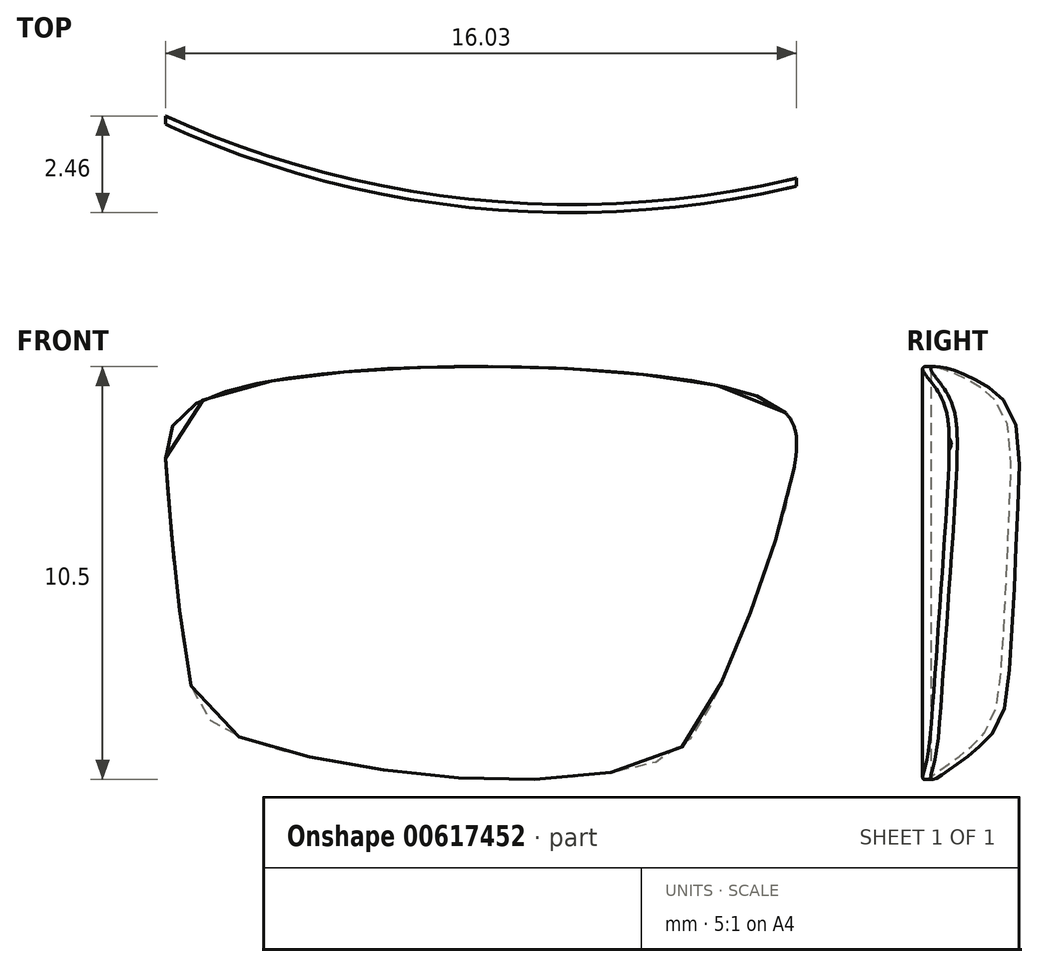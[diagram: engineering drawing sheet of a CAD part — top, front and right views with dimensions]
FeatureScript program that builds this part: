
annotation { "Feature Type Name" : "Feature", "Feature Type Description" : "" }
export const myFeature = defineFeature(function(context is Context, id is Id, definition is map)
    precondition{}
    {
        {
            var Q0;
            Q0=qCreatedBy(makeId("Front.planeOp"),FACE);
            var sketch = newSketch(context, id + "F0", { "sketchPlane" : qUnion([Q0])});
            skFitSpline(sketch, "E0", {"points": [v(-17.91, 1.87) * mm, v(-17.03, 4.08) * mm, v(-2.95, 4.2) * mm, v(-1.99, 2.4) * mm, v(-4.2, -3.82) * mm, v(-5.49, -5.1) * mm, v(-8.7, -5.54) * mm, v(-12.26, -5.32) * mm, v(-16.62, -4.2) * mm, v(-17.4, -2.77) * mm, v(-17.91, 1.87) * mm]});
            skPoint(sketch, "E1", {"position": v(-3.12, 3.22) * mm});
            skLineSegment(sketch, "E2", {"start": v(-2.2, 3.76) * mm, "end": v(-1.25, 3.76) * mm});
            skLineSegment(sketch, "E3", {"start": v(-1.04, 3.56) * mm, "end": v(-1.04, 1.8) * mm});
            skLineSegment(sketch, "E4", {"start": v(-1.15, 1.7) * mm, "end": v(-1.53, 1.7) * mm});
            skLineSegment(sketch, "E5", {"start": v(-1.63, 1.8) * mm, "end": v(-1.63, 2.64) * mm});
            skLineSegment(sketch, "E6", {"start": v(-1.67, 2.66) * mm, "end": v(-1.99, 2.4) * mm});
            skPoint(sketch, "E7.visualSharp", {"position": v(-1.04, 1.7) * mm});
            skArc(sketch, "E7.filletArc", {"start": v(-1.15, 1.7) * mm, "mid": v(-1.07, 1.72) * mm, "end": v(-1.04, 1.8) * mm});
            skPoint(sketch, "E8.visualSharp", {"position": v(-1.63, 1.7) * mm});
            skArc(sketch, "E8.filletArc", {"start": v(-1.63, 1.8) * mm, "mid": v(-1.6, 1.72) * mm, "end": v(-1.53, 1.7) * mm});
            skPoint(sketch, "E9.visualSharp", {"position": v(-1.63, 2.7) * mm});
            skArc(sketch, "E9.filletArc", {"start": v(-1.63, 2.64) * mm, "mid": v(-1.64, 2.67) * mm, "end": v(-1.67, 2.66) * mm});
            skPoint(sketch, "E10.visualSharp", {"position": v(-1.04, 3.76) * mm});
            skArc(sketch, "E10.filletArc", {"start": v(-1.04, 3.56) * mm, "mid": v(-1.1, 3.7) * mm, "end": v(-1.25, 3.76) * mm});
            skSolve(sketch);
        }
        {
            var Q0;
            Q0=qCreatedBy(makeId("Front.planeOp"),FACE);
            var sketch = newSketch(context, id + "F1", { "sketchPlane" : qUnion([Q0])});
            skFitSpline(sketch, "E11.1", {"points": [v(-17.61, 2.35) * mm, v(-17.55, 1.78) * mm, v(-17.49, 1.13) * mm, v(-17.39, 0.2) * mm, v(-17.24, -1.03) * mm, v(-17.09, -2.15) * mm, v(-16.96, -2.88) * mm, v(-16.87, -3.3) * mm, v(-16.76, -3.6) * mm, v(-16.62, -3.8) * mm, v(-16.4, -3.99) * mm, v(-16, -4.19) * mm, v(-15.47, -4.38) * mm, v(-14.85, -4.54) * mm, v(-14.16, -4.7) * mm, v(-13.2, -4.86) * mm, v(-12, -5.02) * mm, v(-10.8, -5.14) * mm, v(-9.72, -5.2) * mm, v(-8.62, -5.18) * mm, v(-7.41, -5.1) * mm, v(-6.46, -4.96) * mm, v(-5.82, -4.8) * mm, v(-5.44, -4.67) * mm, v(-5.17, -4.52) * mm, v(-4.95, -4.34) * mm, v(-4.74, -4.07) * mm, v(-4.5, -3.66) * mm, v(-4.22, -3.09) * mm, v(-3.82, -2.16) * mm, v(-3.4, -1.07) * mm, v(-3.03, 0.06) * mm, v(-2.78, 0.88) * mm, v(-2.57, 1.66) * mm, v(-2.42, 2.35) * mm, v(-2.33, 2.91) * mm, v(-2.34, 3.23) * mm, v(-2.4, 3.4) * mm, v(-2.45, 3.5) * mm, v(-2.53, 3.6) * mm, v(-2.71, 3.75) * mm, v(-3.1, 3.93) * mm, v(-3.86, 4.13) * mm, v(-4.85, 4.3) * mm, v(-6.02, 4.42) * mm, v(-7.31, 4.5) * mm, v(-9.15, 4.56) * mm, v(-11.07, 4.53) * mm, v(-12.9, 4.42) * mm, v(-14.16, 4.28) * mm, v(-15.3, 4.1) * mm, v(-16.24, 3.88) * mm, v(-16.95, 3.62) * mm, v(-17.34, 3.35) * mm, v(-17.52, 3.1) * mm, v(-17.6, 2.79) * mm, v(-17.61, 2.35) * mm, v(-17.55, 1.78) * mm, v(-17.49, 1.13) * mm]});
            skFitSpline(sketch, "E12", {"points": [v(-5.23, 4.33) * mm, v(-3.14, 3.17) * mm, v(-3.05, 0) * mm], "startDerivative": vector(6.83, -0.85) * mm, "endDerivative": vector(-2.66, -9.5) * mm});
            skFitSpline(sketch, "E13", {"points": [v(-17.5, 1.25) * mm, v(-15.83, 3.98) * mm], "startDerivative": vector(-0.72, 7.51) * mm, "endDerivative": vector(1, 0.26) * mm});
            skFitSpline(sketch, "E14", {"points": [v(-17.61, 2.35) * mm, v(-17.55, 1.78) * mm, v(-17.49, 1.13) * mm, v(-17.39, 0.2) * mm, v(-17.24, -1.03) * mm, v(-17.09, -2.15) * mm, v(-16.96, -2.88) * mm, v(-16.87, -3.3) * mm, v(-16.76, -3.6) * mm, v(-16.62, -3.8) * mm, v(-16.4, -3.99) * mm, v(-16, -4.19) * mm, v(-15.47, -4.38) * mm, v(-14.85, -4.54) * mm, v(-14.16, -4.7) * mm, v(-13.2, -4.86) * mm, v(-12, -5.02) * mm, v(-10.8, -5.14) * mm, v(-9.72, -5.2) * mm, v(-8.62, -5.18) * mm, v(-7.41, -5.1) * mm, v(-6.46, -4.96) * mm, v(-5.82, -4.8) * mm, v(-5.44, -4.67) * mm, v(-5.17, -4.52) * mm, v(-4.95, -4.34) * mm, v(-4.74, -4.07) * mm, v(-4.5, -3.66) * mm, v(-4.22, -3.09) * mm, v(-3.82, -2.16) * mm, v(-3.4, -1.07) * mm, v(-3.03, 0.06) * mm, v(-2.78, 0.88) * mm, v(-2.57, 1.66) * mm, v(-2.42, 2.35) * mm, v(-2.33, 2.91) * mm, v(-2.34, 3.23) * mm, v(-2.4, 3.4) * mm, v(-2.45, 3.5) * mm, v(-2.53, 3.6) * mm, v(-2.71, 3.75) * mm, v(-3.1, 3.93) * mm, v(-3.86, 4.13) * mm, v(-4.85, 4.3) * mm, v(-6.02, 4.42) * mm, v(-7.31, 4.5) * mm, v(-9.15, 4.56) * mm, v(-11.07, 4.53) * mm, v(-12.9, 4.42) * mm, v(-14.16, 4.28) * mm, v(-15.3, 4.1) * mm, v(-16.24, 3.88) * mm, v(-16.95, 3.62) * mm, v(-17.34, 3.35) * mm, v(-17.52, 3.1) * mm, v(-17.6, 2.79) * mm, v(-17.61, 2.35) * mm, v(-17.55, 1.78) * mm, v(-17.49, 1.13) * mm]});
            skFitSpline(sketch, "E15", {"points": [v(-3.81, -4.29) * mm, v(-1.38, 0.76) * mm, v(-1.6, 0.87) * mm, v(-1.7, 1.14) * mm, v(-0.52, 1.5) * mm], "startDerivative": vector(10.25, 18.32) * mm, "endDerivative": vector(8.4, 0.03) * mm});
            skLineSegment(sketch, "E16", {"start": v(-0.57, 4.2) * mm, "end": v(-0.57, 4.2) * mm});
            skLineSegment(sketch, "E17", {"start": v(-0.57, 4.2) * mm, "end": v(-0.57, 1.5) * mm});
            skFitSpline(sketch, "E18", {"points": [v(-0.57, 4.2) * mm, v(-1.74, 4) * mm], "startDerivative": vector(-1.49, -0.02) * mm, "endDerivative": vector(-0.6, -0.33) * mm});
            skLineSegment(sketch, "E19", {"start": v(-19.77, 3.41) * mm, "end": v(-19.75, 1.7) * mm});
            skLineSegment(sketch, "E20", {"start": v(-18.95, 1.45) * mm, "end": v(-19.5, 1.44) * mm});
            skLineSegment(sketch, "E21", {"start": v(-18.5, 3.69) * mm, "end": v(-19.52, 3.67) * mm});
            skArc(sketch, "E22.filletArc", {"start": v(-18.5, 3.69) * mm, "mid": v(-18.27, 3.74) * mm, "end": v(-18.1, 3.89) * mm});
            skPoint(sketch, "E23.visualSharp", {"position": v(-19.77, 3.67) * mm});
            skArc(sketch, "E23.filletArc", {"start": v(-19.52, 3.67) * mm, "mid": v(-19.7, 3.6) * mm, "end": v(-19.77, 3.41) * mm});
            skPoint(sketch, "E24.visualSharp", {"position": v(-19.74, 1.25) * mm});
            skArc(sketch, "E25.filletArc", {"start": v(-1.9, 4.17) * mm, "mid": v(-1.73, 4.08) * mm, "end": v(-1.53, 4.08) * mm});
            skFitSpline(sketch, "E26", {"points": [v(-18.1, 3.89) * mm, v(-17.45, 4.45) * mm, v(-12.76, 5.38) * mm, v(-4.33, 5.05) * mm, v(-2.37, 4.5) * mm], "startDerivative": vector(5.74, 6.16) * mm, "endDerivative": vector(8.17, -3.37) * mm});
            skFitSpline(sketch, "E27", {"points": [v(-3.81, -4.29) * mm, v(-4.85, -5.44) * mm, v(-10.17, -6.1) * mm, v(-15.6, -5.22) * mm, v(-17.46, -4.2) * mm, v(-18.48, 1.46) * mm], "startDerivative": vector(-7.7, -11.8) * mm, "endDerivative": vector(-2.7, 30.17) * mm});
            skArc(sketch, "E28.filletArc", {"start": v(-19.75, 1.7) * mm, "mid": v(-19.67, 1.52) * mm, "end": v(-19.5, 1.44) * mm});
            skArc(sketch, "E29.filletArc", {"start": v(-18.44, 0.99) * mm, "mid": v(-18.6, 1.32) * mm, "end": v(-18.95, 1.45) * mm});
            skArc(sketch, "E30.MirrorCS", {"start": v(18.61, 1.7) * mm, "mid": v(18.54, 1.52) * mm, "end": v(18.36, 1.45) * mm});
            skArc(sketch, "E31.MirrorCS", {"start": v(17.36, 3.69) * mm, "mid": v(17.14, 3.74) * mm, "end": v(16.96, 3.9) * mm});
            skArc(sketch, "E32.MirrorCS", {"start": v(0.76, 4.17) * mm, "mid": v(0.59, 4.08) * mm, "end": v(0.4, 4.08) * mm});
            skArc(sketch, "E33.MirrorCS", {"start": v(17.3, 1) * mm, "mid": v(17.47, 1.32) * mm, "end": v(17.82, 1.45) * mm});
            skArc(sketch, "E34.MirrorCS", {"start": v(18.39, 3.67) * mm, "mid": v(18.56, 3.6) * mm, "end": v(18.64, 3.42) * mm});
            skLineSegment(sketch, "E35.MirrorCS", {"start": v(17.82, 1.45) * mm, "end": v(18.36, 1.45) * mm});
            skFitSpline(sketch, "E36.MirrorCS", {"points": [v(-0.57, 4.2) * mm, v(0.6, 4) * mm], "startDerivative": vector(1.49, -0.02) * mm, "endDerivative": vector(0.6, -0.33) * mm});
            skLineSegment(sketch, "E37.MirrorCS", {"start": v(17.36, 3.69) * mm, "end": v(18.39, 3.67) * mm});
            skFitSpline(sketch, "E38.MirrorCS", {"points": [v(2.68, -4.29) * mm, v(3.72, -5.44) * mm, v(9.04, -6.1) * mm, v(14.47, -5.22) * mm, v(16.32, -4.2) * mm, v(17.35, 1.46) * mm], "startDerivative": vector(7.7, -11.79) * mm, "endDerivative": vector(2.69, 30.18) * mm});
            skFitSpline(sketch, "E39.MirrorCS", {"points": [v(4.1, 4.33) * mm, v(2, 3.17) * mm, v(1.92, 0) * mm], "startDerivative": vector(-6.83, -0.85) * mm, "endDerivative": vector(2.66, -9.5) * mm});
            skPoint(sketch, "E40.MirrorP", {"position": v(18.6, 1.25) * mm});
            skFitSpline(sketch, "E41.MirrorCS", {"points": [v(16.36, 1.25) * mm, v(14.7, 3.98) * mm], "startDerivative": vector(0.72, 7.51) * mm, "endDerivative": vector(-1, 0.26) * mm});
            skLineSegment(sketch, "E42.MirrorCS", {"start": v(18.64, 3.42) * mm, "end": v(18.61, 1.7) * mm});
            skFitSpline(sketch, "E43.MirrorCS", {"points": [v(16.48, 2.35) * mm, v(16.42, 1.79) * mm, v(16.35, 1.13) * mm, v(16.25, 0.2) * mm, v(16.1, -1.02) * mm, v(15.95, -2.14) * mm, v(15.83, -2.88) * mm, v(15.73, -3.3) * mm, v(15.62, -3.6) * mm, v(15.48, -3.8) * mm, v(15.26, -3.99) * mm, v(14.87, -4.19) * mm, v(14.34, -4.37) * mm, v(13.71, -4.54) * mm, v(13.03, -4.69) * mm, v(12.07, -4.86) * mm, v(10.87, -5.02) * mm, v(9.67, -5.14) * mm, v(8.58, -5.2) * mm, v(7.5, -5.18) * mm, v(6.28, -5.1) * mm, v(5.33, -4.95) * mm, v(4.69, -4.8) * mm, v(4.3, -4.67) * mm, v(4.03, -4.52) * mm, v(3.82, -4.34) * mm, v(3.6, -4.07) * mm, v(3.36, -3.66) * mm, v(3.09, -3.09) * mm, v(2.69, -2.16) * mm, v(2.27, -1.07) * mm, v(1.9, 0.06) * mm, v(1.64, 0.88) * mm, v(1.43, 1.66) * mm, v(1.28, 2.35) * mm, v(1.2, 2.91) * mm, v(1.2, 3.23) * mm, v(1.26, 3.4) * mm, v(1.31, 3.5) * mm, v(1.4, 3.6) * mm, v(1.58, 3.75) * mm, v(1.96, 3.93) * mm, v(2.73, 4.13) * mm, v(3.72, 4.3) * mm, v(4.88, 4.42) * mm, v(6.18, 4.5) * mm, v(8.02, 4.56) * mm, v(9.94, 4.54) * mm, v(11.76, 4.42) * mm, v(13.03, 4.28) * mm, v(14.16, 4.1) * mm, v(15.1, 3.88) * mm, v(15.8, 3.62) * mm, v(16.2, 3.35) * mm, v(16.38, 3.1) * mm, v(16.47, 2.79) * mm, v(16.48, 2.35) * mm, v(16.42, 1.79) * mm, v(16.35, 1.13) * mm]});
            skFitSpline(sketch, "E44.MirrorCS", {"points": [v(16.96, 3.9) * mm, v(16.3, 4.45) * mm, v(11.63, 5.39) * mm, v(3.19, 5.05) * mm, v(1.23, 4.5) * mm], "startDerivative": vector(-5.74, 6.15) * mm, "endDerivative": vector(-8.17, -3.38) * mm});
            skPoint(sketch, "E45.MirrorP", {"position": v(18.64, 3.67) * mm});
            skFitSpline(sketch, "E46.MirrorCS", {"points": [v(16.48, 2.35) * mm, v(16.42, 1.79) * mm, v(16.35, 1.13) * mm, v(16.25, 0.2) * mm, v(16.1, -1.02) * mm, v(15.95, -2.14) * mm, v(15.83, -2.88) * mm, v(15.73, -3.3) * mm, v(15.62, -3.6) * mm, v(15.48, -3.8) * mm, v(15.26, -3.99) * mm, v(14.87, -4.19) * mm, v(14.34, -4.37) * mm, v(13.71, -4.54) * mm, v(13.03, -4.69) * mm, v(12.07, -4.86) * mm, v(10.87, -5.02) * mm, v(9.67, -5.14) * mm, v(8.58, -5.2) * mm, v(7.5, -5.18) * mm, v(6.28, -5.1) * mm, v(5.33, -4.95) * mm, v(4.69, -4.8) * mm, v(4.3, -4.67) * mm, v(4.03, -4.52) * mm, v(3.82, -4.34) * mm, v(3.6, -4.07) * mm, v(3.36, -3.66) * mm, v(3.09, -3.09) * mm, v(2.69, -2.16) * mm, v(2.27, -1.07) * mm, v(1.9, 0.06) * mm, v(1.64, 0.88) * mm, v(1.43, 1.66) * mm, v(1.28, 2.35) * mm, v(1.2, 2.91) * mm, v(1.2, 3.23) * mm, v(1.26, 3.4) * mm, v(1.31, 3.5) * mm, v(1.4, 3.6) * mm, v(1.58, 3.75) * mm, v(1.96, 3.93) * mm, v(2.73, 4.13) * mm, v(3.72, 4.3) * mm, v(4.88, 4.42) * mm, v(6.18, 4.5) * mm, v(8.02, 4.56) * mm, v(9.94, 4.54) * mm, v(11.76, 4.42) * mm, v(13.03, 4.28) * mm, v(14.16, 4.1) * mm, v(15.1, 3.88) * mm, v(15.8, 3.62) * mm, v(16.2, 3.35) * mm, v(16.38, 3.1) * mm, v(16.47, 2.79) * mm, v(16.48, 2.35) * mm, v(16.42, 1.79) * mm, v(16.35, 1.13) * mm]});
            skFitSpline(sketch, "E47.MirrorCS", {"points": [v(2.68, -4.29) * mm, v(0.24, 0.76) * mm, v(0.46, 0.87) * mm, v(0.57, 1.14) * mm, v(-0.61, 1.5) * mm], "startDerivative": vector(-10.26, 18.32) * mm, "endDerivative": vector(-8.4, 0.03) * mm});
            skFitSpline(sketch, "E48", {"points": [v(-1.9, 4.17) * mm, v(-2.37, 4.5) * mm], "startDerivative": vector(-0.43, 0.42) * mm, "endDerivative": vector(-0.55, 0.25) * mm});
            skFitSpline(sketch, "E49.MirrorCS", {"points": [v(0.76, 4.17) * mm, v(1.23, 4.5) * mm], "startDerivative": vector(0.43, 0.42) * mm, "endDerivative": vector(0.55, 0.25) * mm});
            skSolve(sketch);
        }
        {
            var Q0;
            Q0=qCreatedBy(makeId("Top.planeOp"),FACE);
            var sketch = newSketch(context, id + "F2", { "sketchPlane" : qUnion([Q0])});
            skPoint(sketch, "E50", {"position": v(-17.98, 0) * mm});
            skPoint(sketch, "E51", {"position": v(-1.93, 0) * mm});
            skLineSegment(sketch, "E52", {"start": v(-17.98, 0) * mm, "end": v(-1.93, 0) * mm});
            skArc(sketch, "E53", {"start": v(-17.98, 4.42) * mm, "mid": v(-10.09, 2.28) * mm, "end": v(-1.93, 2.84) * mm});
            skLineSegment(sketch, "E54", {"start": v(-17.98, 4.42) * mm, "end": v(-17.96, 4.62) * mm});
            skLineSegment(sketch, "E55", {"start": v(-1.93, 2.84) * mm, "end": v(-1.91, 3.04) * mm});
            skArc(sketch, "E56", {"start": v(-17.96, 4.62) * mm, "mid": v(-10.08, 2.5) * mm, "end": v(-1.93, 3.04) * mm});
            skLineSegment(sketch, "E57", {"start": v(-1.93, 3.04) * mm, "end": v(-1.91, 3.04) * mm});
            skArc(sketch, "E58", {"start": v(-18.5, 5.51) * mm, "mid": v(-10.28, 3.09) * mm, "end": v(-1.74, 3.67) * mm});
            skArc(sketch, "E59", {"start": v(-18.5, 4.3) * mm, "mid": v(-10.27, 1.98) * mm, "end": v(-1.74, 2.55) * mm});
            skLineSegment(sketch, "E60", {"start": v(-18.5, 4.3) * mm, "end": v(-19.77, 4.46) * mm});
            skLineSegment(sketch, "E61", {"start": v(-18.5, 5.51) * mm, "end": v(-19.77, 5.67) * mm});
            skLineSegment(sketch, "E62", {"start": v(-19.77, 4.46) * mm, "end": v(-19.77, 5.67) * mm});
            skArc(sketch, "E63", {"start": v(-1.74, 2.55) * mm, "mid": v(-1.17, 2.36) * mm, "end": v(-0.57, 2.35) * mm});
            skArc(sketch, "E64", {"start": v(-1.74, 3.67) * mm, "mid": v(-1.21, 3.28) * mm, "end": v(-0.57, 3.15) * mm});
            skLineSegment(sketch, "E65", {"start": v(-0.57, 2.35) * mm, "end": v(-0.57, 3.15) * mm});
            skSolve(sketch);
        }
        {
            var Q0;
            Q0=makeQuery(id+"F2.imprint","IMPRINT",FACE,{"disambiguationData":[TD([[makeQuery(id+"F2.imprint","IMPRINT",EDGE,{"derivedFrom":sQuery(id+"F2.wireOp",EDGE,"E53")}),1.0]])]});
            extrude(context, id + "F3", {"entities" : qUnion([Q0]), "endBound" : BoundingType.SYMMETRIC, "depth" : 25.4 * mm, "offsetDistance" : 25.4 * mm});
        }
        {
            var Q0;
            {var subQ0=sQuery(id+"F0.wireOp",EDGE,"E0");var subQ1=makeQuery(id+"F0.imprint","INTERSECT",VERTEX,{"derivedFrom":[subQ0,sQuery(id+"F0.wireOp",EDGE,"E2")]});Q0=makeQuery(id+"F0.imprint","IMPRINT",FACE,{"disambiguationData":[TD([[makeQuery(id+"F0.imprint","IMPRINT",EDGE,{"disambiguationData":[TD([[subQ1,-1.0]])],"derivedFrom":subQ0}),-1.0]])]});}
            extrude(context, id + "F4", {"entities" : qUnion([Q0]), "oppositeDirection" : true, "depth" : 25.4 * mm, "offsetDistance" : 25.4 * mm});
        }
        {
            var Q0;
            Q0=makeQuery(id+"F4.opExtrude","SWEPT_BODY",BODY,{"disambiguationData":[OSD([sQuery(id+"F0.wireOp",EDGE,"E0")])]});
            var Q1;
            Q1=makeQuery(id+"F3.opExtrude","SWEPT_BODY",BODY,{"disambiguationData":[OSD([sQuery(id+"F2.wireOp",EDGE,"E53"),sQuery(id+"F2.wireOp",EDGE,"E54"),sQuery(id+"F2.wireOp",EDGE,"E55"),sQuery(id+"F2.wireOp",EDGE,"E56"),sQuery(id+"F2.wireOp",EDGE,"E57")])]});
            booleanBodies(context, id + "F5", {"operationType" : BooleanOperationType.INTERSECTION, "tools" : qUnion([Q0, Q1])});
        }
    });
